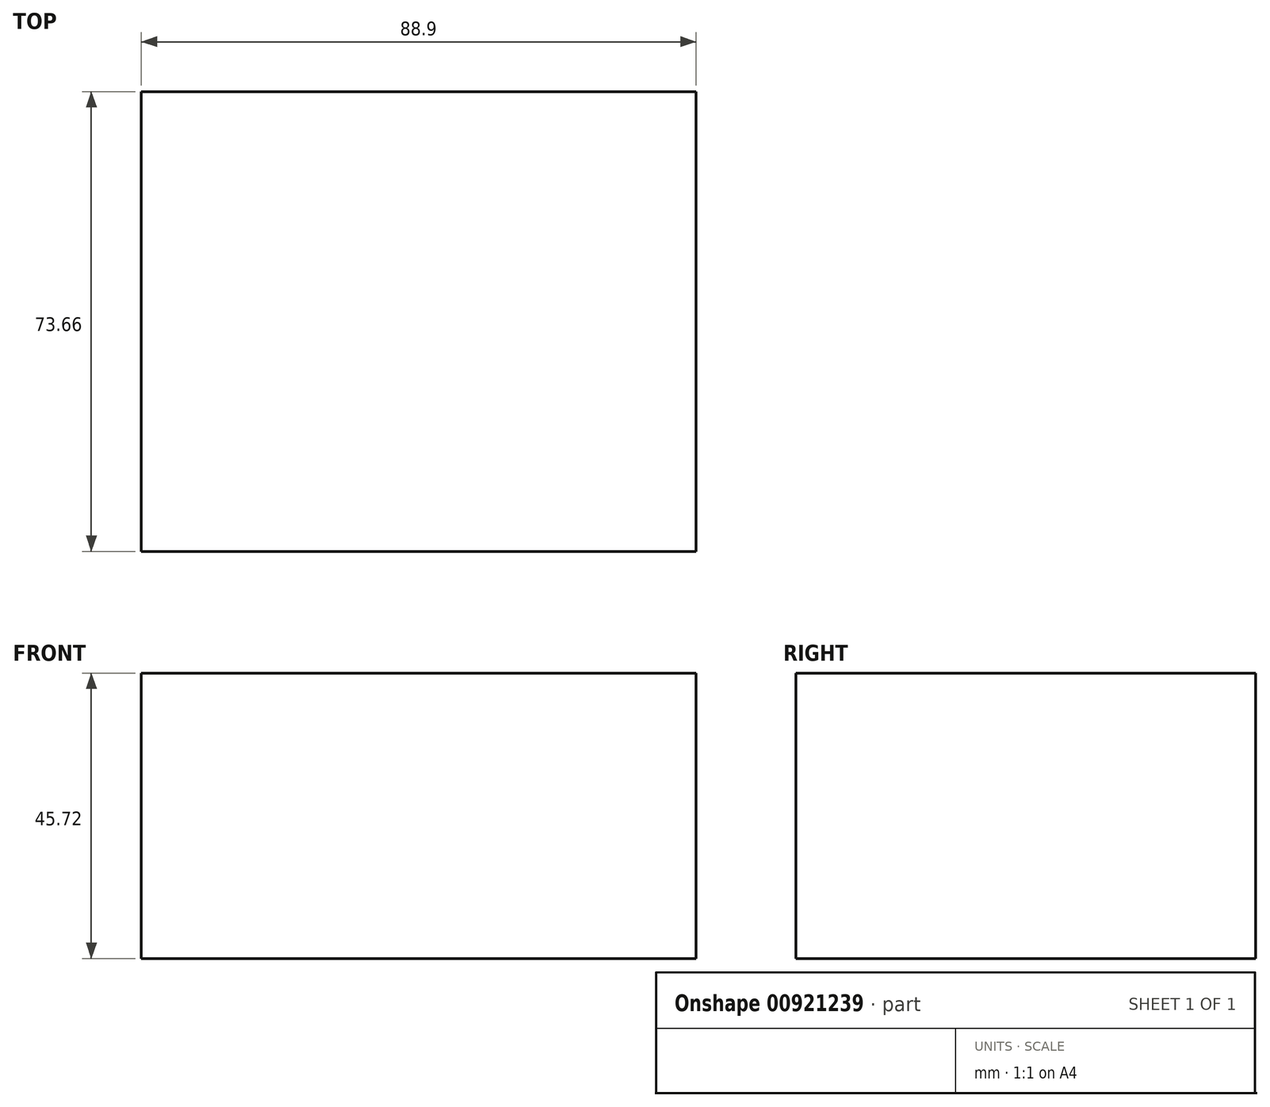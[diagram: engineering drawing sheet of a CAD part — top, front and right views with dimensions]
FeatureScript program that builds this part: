
annotation { "Feature Type Name" : "Feature", "Feature Type Description" : "" }
export const myFeature = defineFeature(function(context is Context, id is Id, definition is map)
    precondition{}
    {
        {
            var Q0;
            Q0=qCreatedBy(makeId("Top.planeOp"),FACE);
            var sketch = newSketch(context, id + "F0", { "sketchPlane" : qUnion([Q0])});
            skLineSegment(sketch, "E0.bottom", {"start": v(44.45, 36.83) * mm, "end": v(-44.45, 36.83) * mm});
            skLineSegment(sketch, "E0.top", {"start": v(44.45, -36.83) * mm, "end": v(-44.45, -36.83) * mm});
            skLineSegment(sketch, "E0.left", {"start": v(44.45, 36.83) * mm, "end": v(44.45, -36.83) * mm});
            skLineSegment(sketch, "E0.right", {"start": v(-44.45, 36.83) * mm, "end": v(-44.45, -36.83) * mm});
            skPoint(sketch, "E0.middle", {"position": v(0, 0) * mm});
            skSolve(sketch);
        }
        {
            var Q0;
            Q0 = qSketchRegion(id + "F0", true);
            extrude(context, id + "F1", {"entities" : qUnion([Q0]), "depth" : 45.72 * mm, "offsetDistance" : 25.4 * mm});
        }
    });
